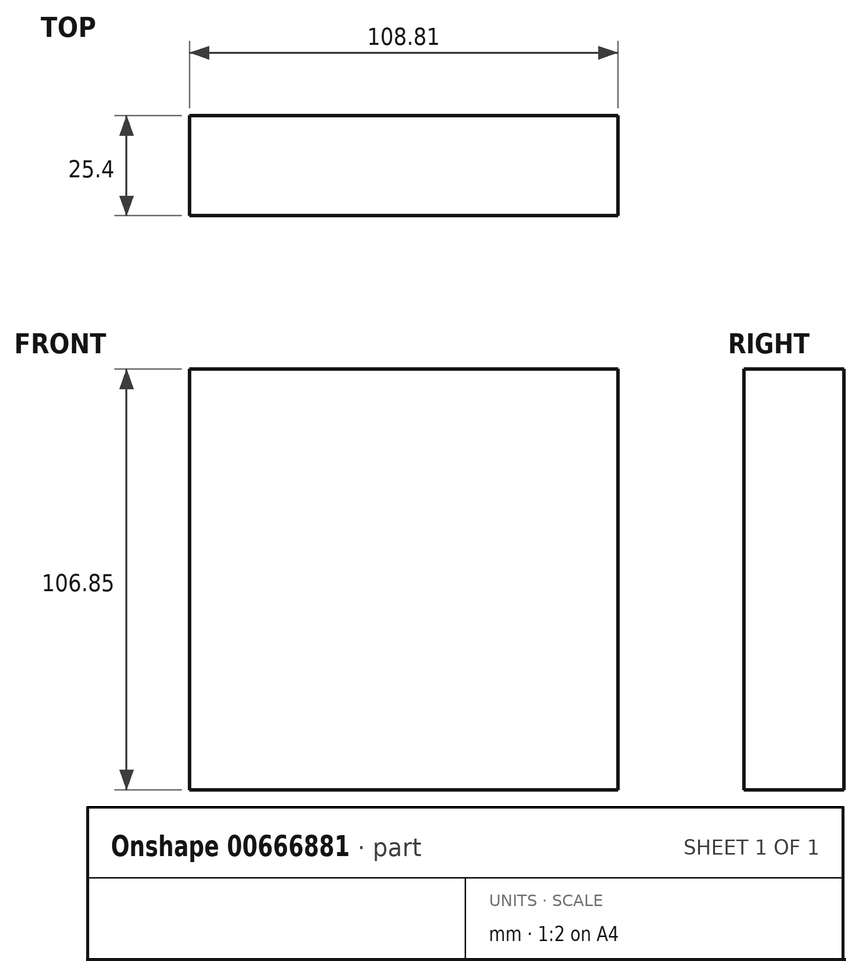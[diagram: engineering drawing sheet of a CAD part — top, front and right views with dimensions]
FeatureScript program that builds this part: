
annotation { "Feature Type Name" : "Feature", "Feature Type Description" : "" }
export const myFeature = defineFeature(function(context is Context, id is Id, definition is map)
    precondition{}
    {
        {
            var Q0;
            Q0=qCreatedBy(makeId("Front.planeOp"),FACE);
            var sketch = newSketch(context, id + "F0", { "sketchPlane" : qUnion([Q0])});
            skLineSegment(sketch, "E0.bottom", {"start": v(-56.75, 57.44) * mm, "end": v(52.06, 57.44) * mm});
            skLineSegment(sketch, "E0.top", {"start": v(-56.75, -49.4) * mm, "end": v(52.06, -49.4) * mm});
            skLineSegment(sketch, "E0.left", {"start": v(-56.75, 57.44) * mm, "end": v(-56.75, -49.4) * mm});
            skLineSegment(sketch, "E0.right", {"start": v(52.06, 57.44) * mm, "end": v(52.06, -49.4) * mm});
            skSolve(sketch);
        }
        {
            var Q0;
            Q0 = qSketchRegion(id + "F0", true);
            extrude(context, id + "F1", {"entities" : qUnion([Q0]), "depth" : 25.4 * mm, "offsetDistance" : 25.4 * mm});
        }
    });
